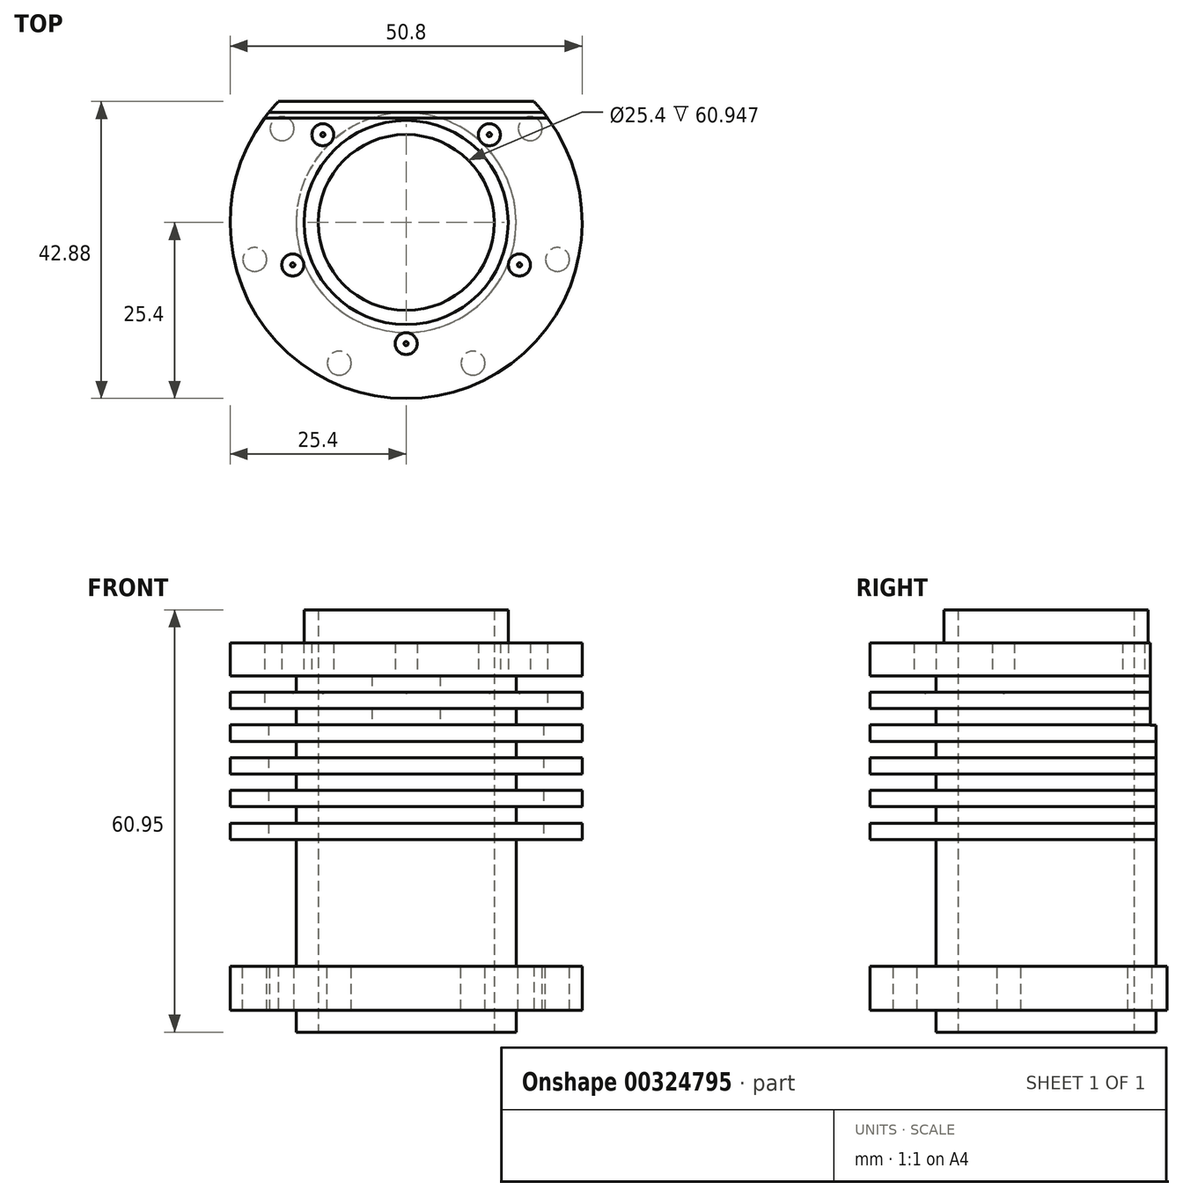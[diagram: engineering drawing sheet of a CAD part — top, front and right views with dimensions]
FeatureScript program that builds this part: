
annotation { "Feature Type Name" : "Feature", "Feature Type Description" : "" }
export const myFeature = defineFeature(function(context is Context, id is Id, definition is map)
    precondition{}
    {
        {
            var Q0;
            Q0=qCreatedBy(makeId("Top.planeOp"),FACE);
            var sketch = newSketch(context, id + "F0", { "sketchPlane" : qUnion([Q0])});
            skCircle(sketch, "E0", {"center": v(0, 0) * mm, "radius": 25.4 * mm});
            skSolve(sketch);
        }
        {
            var Q0;
            Q0=makeQuery(id+"F0.imprint","IMPRINT",FACE,{"disambiguationData":[TD([[makeQuery(id+"F0.imprint","IMPRINT",EDGE,{"derivedFrom":sQuery(id+"F0.wireOp",EDGE,"E0")}),1.0]])]});
            extrude(context, id + "F1", {"entities" : qUnion([Q0]), "depth" : 53 * mm, "offsetDistance" : 25.4 * mm});
        }
        {
            var Q0;
            Q0=makeQuery(id+"F1.opExtrude","CAP_FACE",FACE,{"disambiguationData":[OSD([sQuery(id+"F0.wireOp",EDGE,"E0")])],"isStart":false});
            var sketch = newSketch(context, id + "F2", { "sketchPlane" : qUnion([Q0])});
            skCircle(sketch, "E1", {"center": v(0, 0) * mm, "radius": 14.73 * mm});
            skSolve(sketch);
        }
        {
            var Q0;
            Q0=makeQuery(id+"F2.imprint","IMPRINT",FACE,{"disambiguationData":[TD([[makeQuery(id+"F2.imprint","IMPRINT",EDGE,{"derivedFrom":sQuery(id+"F2.wireOp",EDGE,"E1")}),1.0]])]});
            extrude(context, id + "F3", {"entities" : qUnion([Q0]), "operationType" : NewBodyOperationType.ADD, "depth" : 4.76 * mm, "offsetDistance" : 25.4 * mm});
        }
        {
            var Q0;
            Q0=makeQuery(id+"F1.opExtrude","CAP_FACE",FACE,{"disambiguationData":[OSD([sQuery(id+"F0.wireOp",EDGE,"E0")])],"isStart":true});
            var sketch = newSketch(context, id + "F4", { "sketchPlane" : qUnion([Q0])});
            skCircle(sketch, "E2", {"center": v(0, 0) * mm, "radius": 15.88 * mm});
            skSolve(sketch);
        }
        {
            var Q0;
            Q0=makeQuery(id+"F4.imprint","IMPRINT",FACE,{"disambiguationData":[TD([[makeQuery(id+"F4.imprint","IMPRINT",EDGE,{"derivedFrom":sQuery(id+"F4.wireOp",EDGE,"E2")}),1.0]])]});
            extrude(context, id + "F5", {"entities" : qUnion([Q0]), "operationType" : NewBodyOperationType.ADD, "depth" : 3.17 * mm, "offsetDistance" : 25.4 * mm});
        }
        {
            var Q0;
            Q0=makeQuery(id+"F5.opExtrude","CAP_FACE",FACE,{"disambiguationData":[OSD([sQuery(id+"F4.wireOp",EDGE,"E2")])],"isStart":false});
            var sketch = newSketch(context, id + "F6", { "sketchPlane" : qUnion([Q0])});
            skSolve(sketch);
        }
        {
            var Q0;
            Q0=makeQuery(id+"F6.imprint","IMPRINT",FACE,{"disambiguationData":[TD([[makeQuery(id+"F6.imprint","IMPRINT",EDGE,{"derivedFrom":makeQuery(id+"F5.opExtrude","CAP_EDGE",EDGE,{"disambiguationData":[OSD([sQuery(id+"F4.wireOp",EDGE,"E2")])],"isStart":false})}),1.0]])]});
            var sketch = newSketch(context, id + "F7", { "sketchPlane" : qUnion([Q0])});
            skCircle(sketch, "E3", {"center": v(0, 0) * mm, "radius": 12.7 * mm});
            skSolve(sketch);
        }
        {
            var Q0;
            Q0=makeQuery(id+"F7.imprint","IMPRINT",FACE,{"disambiguationData":[TD([[makeQuery(id+"F7.imprint","IMPRINT",EDGE,{"derivedFrom":sQuery(id+"F7.wireOp",EDGE,"E3")}),1.0]])]});
            extrude(context, id + "F8", {"entities" : qUnion([Q0]), "operationType" : NewBodyOperationType.REMOVE, "endBound" : BoundingType.THROUGH_ALL, "oppositeDirection" : true, "depth" : 25.4 * mm, "offsetDistance" : 25.4 * mm});
        }
        {
            var Q0;
            Q0=qCreatedBy(makeId("Front.planeOp"),FACE);
            var sketch = newSketch(context, id + "F9", { "sketchPlane" : qUnion([Q0])});
            skLineSegment(sketch, "E4", {"start": v(15.88, 63.37) * mm, "end": v(15.88, -10.47) * mm, "construction": true});
            skLineSegment(sketch, "E5", {"start": v(-43.89, 48.25) * mm, "end": v(39.02, 48.25) * mm, "construction": true});
            skLineSegment(sketch, "E6.bottom", {"start": v(15.88, 48.25) * mm, "end": v(28.02, 48.25) * mm});
            skLineSegment(sketch, "E6.top", {"start": v(15.88, 45.89) * mm, "end": v(28.02, 45.89) * mm});
            skLineSegment(sketch, "E6.left", {"start": v(15.88, 48.25) * mm, "end": v(15.88, 45.89) * mm});
            skLineSegment(sketch, "E6.right", {"start": v(28.02, 48.25) * mm, "end": v(28.02, 45.89) * mm});
            skLineSegment(sketch, "E7.1.0.0", {"start": v(15.88, 43.52) * mm, "end": v(28.02, 43.52) * mm});
            skLineSegment(sketch, "E7.1.0.1", {"start": v(15.88, 41.16) * mm, "end": v(28.02, 41.16) * mm});
            skLineSegment(sketch, "E7.1.0.2", {"start": v(15.88, 43.52) * mm, "end": v(15.88, 41.16) * mm});
            skLineSegment(sketch, "E7.1.0.3", {"start": v(28.02, 43.52) * mm, "end": v(28.02, 41.16) * mm});
            skLineSegment(sketch, "E7.2.0.0", {"start": v(15.88, 38.8) * mm, "end": v(28.02, 38.8) * mm});
            skLineSegment(sketch, "E7.2.0.1", {"start": v(15.88, 36.44) * mm, "end": v(28.02, 36.44) * mm});
            skLineSegment(sketch, "E7.2.0.2", {"start": v(15.88, 38.8) * mm, "end": v(15.88, 36.44) * mm});
            skLineSegment(sketch, "E7.2.0.3", {"start": v(28.02, 38.8) * mm, "end": v(28.02, 36.44) * mm});
            skLineSegment(sketch, "E7.3.0.0", {"start": v(15.88, 34.07) * mm, "end": v(28.02, 34.07) * mm});
            skLineSegment(sketch, "E7.3.0.1", {"start": v(15.88, 31.71) * mm, "end": v(28.02, 31.71) * mm});
            skLineSegment(sketch, "E7.3.0.2", {"start": v(15.88, 34.07) * mm, "end": v(15.88, 31.71) * mm});
            skLineSegment(sketch, "E7.3.0.3", {"start": v(28.02, 34.07) * mm, "end": v(28.02, 31.71) * mm});
            skLineSegment(sketch, "E7.4.0.0", {"start": v(15.88, 29.35) * mm, "end": v(28.02, 29.35) * mm});
            skLineSegment(sketch, "E7.4.0.1", {"start": v(15.88, 26.99) * mm, "end": v(28.02, 26.99) * mm});
            skLineSegment(sketch, "E7.4.0.2", {"start": v(15.88, 29.35) * mm, "end": v(15.88, 26.99) * mm});
            skLineSegment(sketch, "E7.4.0.3", {"start": v(28.02, 29.35) * mm, "end": v(28.02, 26.99) * mm});
            skLineSegment(sketch, "E7.direction1", {"start": v(15.88, 45.89) * mm, "end": v(15.88, 41.16) * mm, "construction": true});
            skLineSegment(sketch, "E8", {"start": v(-27.72, 6.35) * mm, "end": v(31.12, 6.35) * mm, "construction": true});
            skLineSegment(sketch, "E9", {"start": v(15.88, 24.63) * mm, "end": v(15.88, 6.35) * mm});
            skLineSegment(sketch, "E10", {"start": v(15.88, 6.35) * mm, "end": v(28.98, 6.35) * mm});
            skSolve(sketch);
        }
        {
            var Q0;
            Q0=makeQuery(id+"F9.imprint","IMPRINT",FACE,{"disambiguationData":[TD([[makeQuery(id+"F9.imprint","IMPRINT",EDGE,{"derivedFrom":sQuery(id+"F9.wireOp",EDGE,"E6.bottom")}),-1.0]])]});
            var Q1;
            Q1=makeQuery(id+"F9.imprint","IMPRINT",FACE,{"disambiguationData":[TD([[makeQuery(id+"F9.imprint","IMPRINT",EDGE,{"derivedFrom":sQuery(id+"F9.wireOp",EDGE,"E7.1.0.0")}),-1.0]])]});
            var Q2;
            Q2=makeQuery(id+"F9.imprint","IMPRINT",FACE,{"disambiguationData":[TD([[makeQuery(id+"F9.imprint","IMPRINT",EDGE,{"derivedFrom":sQuery(id+"F9.wireOp",EDGE,"E7.2.0.0")}),-1.0]])]});
            var Q3;
            Q3=makeQuery(id+"F9.imprint","IMPRINT",FACE,{"disambiguationData":[TD([[makeQuery(id+"F9.imprint","IMPRINT",EDGE,{"derivedFrom":sQuery(id+"F9.wireOp",EDGE,"E7.3.0.0")}),-1.0]])]});
            var Q4;
            Q4=makeQuery(id+"F9.imprint","IMPRINT",FACE,{"disambiguationData":[TD([[makeQuery(id+"F9.imprint","IMPRINT",EDGE,{"derivedFrom":sQuery(id+"F9.wireOp",EDGE,"E7.4.0.0")}),-1.0]])]});
            var Q5;
            Q5=makeQuery(id+"F9.imprint","IMPRINT",FACE,{"disambiguationData":[TD([[makeQuery(id+"F9.imprint","IMPRINT",EDGE,{"derivedFrom":sQuery(id+"F9.wireOp",EDGE,"e0e7658a-f0d1-407f-a81c-850310b283b5.0.5.0")}),-1.0]])]});
            var Q6;
            Q6=makeQuery(id+"F1.opExtrude","SWEPT_FACE",FACE,{"disambiguationData":[OSD([sQuery(id+"F0.wireOp",EDGE,"E0")])]});
            revolve(context, id + "F10", {"operationType" : NewBodyOperationType.REMOVE, "entities" : qUnion([Q0, Q1, Q2, Q3, Q4, Q5]), "axis" : qUnion([Q6]), "revolveType" : RevolveType.FULL, "oppositeDirection" : true});
        }
        {
            var Q0;
            Q0=qCreatedBy(makeId("Front.planeOp"),FACE);
            var sketch = newSketch(context, id + "F11", { "sketchPlane" : qUnion([Q0])});
            skLineSegment(sketch, "E11", {"start": v(-39.25, 6.35) * mm, "end": v(35.32, 6.35) * mm, "construction": true});
            skLineSegment(sketch, "E12", {"start": v(-28.17, 24.63) * mm, "end": v(30.33, 24.63) * mm, "construction": true});
            skLineSegment(sketch, "E13", {"start": v(15.87, 28.26) * mm, "end": v(15.88, -4.44) * mm, "construction": true});
            skLineSegment(sketch, "E14.bottom", {"start": v(15.88, 24.63) * mm, "end": v(29.2, 24.63) * mm});
            skLineSegment(sketch, "E14.top", {"start": v(15.88, 6.35) * mm, "end": v(29.2, 6.35) * mm});
            skLineSegment(sketch, "E14.left", {"start": v(15.88, 24.63) * mm, "end": v(15.88, 6.35) * mm});
            skLineSegment(sketch, "E14.right", {"start": v(29.2, 24.63) * mm, "end": v(29.2, 6.35) * mm});
            skSolve(sketch);
        }
        {
            var Q0;
            Q0=makeQuery(id+"F11.imprint","IMPRINT",FACE,{"disambiguationData":[TD([[makeQuery(id+"F11.imprint","IMPRINT",EDGE,{"derivedFrom":sQuery(id+"F11.wireOp",EDGE,"E14.bottom")}),-1.0]])]});
            var Q1;
            {var subQ0=sQuery(id+"F0.wireOp",EDGE,"E0");Q1=makeQuery(id+"F10.boolean.opBoolean","SPLIT",FACE,{"disambiguationData":[TD([makeQuery(id+"F1.opExtrude","CAP_FACE",FACE,{"disambiguationData":[OSD([subQ0])],"isStart":true})])],"derivedFrom":makeQuery(id+"F1.opExtrude","SWEPT_FACE",FACE,{"disambiguationData":[OSD([subQ0])]})});}
            revolve(context, id + "F12", {"operationType" : NewBodyOperationType.REMOVE, "entities" : qUnion([Q0]), "axis" : qUnion([Q1]), "revolveType" : RevolveType.FULL, "oppositeDirection" : true});
        }
        {
            var Q0;
            Q0=makeQuery(id+"F1.opExtrude","CAP_FACE",FACE,{"disambiguationData":[OSD([sQuery(id+"F0.wireOp",EDGE,"E0")])],"isStart":false});
            var sketch = newSketch(context, id + "F13", { "sketchPlane" : qUnion([Q0])});
            skLineSegment(sketch, "E15.bottom", {"start": v(-28.86, 15.09) * mm, "end": v(35.5, 15.09) * mm});
            skLineSegment(sketch, "E15.top", {"start": v(-28.86, 32.1) * mm, "end": v(35.5, 32.1) * mm});
            skLineSegment(sketch, "E15.left", {"start": v(-28.86, 15.09) * mm, "end": v(-28.86, 32.1) * mm});
            skLineSegment(sketch, "E15.right", {"start": v(35.5, 15.09) * mm, "end": v(35.5, 32.1) * mm});
            skSolve(sketch);
        }
        {
            var Q0;
            Q0=makeQuery(id+"F13.imprint","IMPRINT",FACE,{"disambiguationData":[TD([[makeQuery(id+"F13.imprint","IMPRINT",EDGE,{"derivedFrom":sQuery(id+"F13.wireOp",EDGE,"E15.top")}),-1.0]])]});
            var Q1;
            {var subQ0=sQuery(id+"F13.wireOp",EDGE,"E15.bottom");var subQ1=makeQuery(id+"F1.opExtrude","CAP_EDGE",EDGE,{"disambiguationData":[OSD([sQuery(id+"F0.wireOp",EDGE,"E0")])],"isStart":false});var subQ2=makeQuery(id+"F13.imprint","INTERSECT",VERTEX,{"disambiguationData":[OD(0.0)],"derivedFrom":[subQ1,subQ0]});Q1=makeQuery(id+"F13.imprint","IMPRINT",FACE,{"disambiguationData":[TD([[makeQuery(id+"F13.imprint","IMPRINT",EDGE,{"disambiguationData":[TD([[subQ2,-1.0]])],"derivedFrom":subQ0}),1.0]])]});}
            extrude(context, id + "F14", {"entities" : qUnion([Q0, Q1]), "operationType" : NewBodyOperationType.REMOVE, "oppositeDirection" : true, "depth" : 11.86 * mm, "offsetDistance" : 25.4 * mm});
        }
        {
            var Q0;
            Q0=makeQuery(id+"F14.boolean.opBoolean","COPY",FACE,{"derivedFrom":makeQuery(id+"F14.opExtrude","CAP_FACE",FACE,{"disambiguationData":[OSD([sQuery(id+"F13.wireOp",EDGE,"E15.bottom"),sQuery(id+"F13.wireOp",EDGE,"E15.top"),sQuery(id+"F13.wireOp",EDGE,"E15.left"),sQuery(id+"F13.wireOp",EDGE,"E15.right")])],"isStart":false})});
            var sketch = newSketch(context, id + "F15", { "sketchPlane" : qUnion([Q0])});
            skLineSegment(sketch, "E16.bottom", {"start": v(-23.48, 25.8) * mm, "end": v(22.7, 25.8) * mm});
            skLineSegment(sketch, "E16.top", {"start": v(-23.48, 15.88) * mm, "end": v(22.7, 15.88) * mm});
            skLineSegment(sketch, "E16.left", {"start": v(-23.48, 25.8) * mm, "end": v(-23.48, 15.88) * mm});
            skLineSegment(sketch, "E16.right", {"start": v(22.7, 25.8) * mm, "end": v(22.7, 15.88) * mm});
            skSolve(sketch);
        }
        {
            var Q0;
            Q0=makeQuery(id+"F15.imprint","IMPRINT",FACE,{"disambiguationData":[TD([[makeQuery(id+"F15.imprint","IMPRINT",EDGE,{"derivedFrom":sQuery(id+"F15.wireOp",EDGE,"E16.bottom")}),-1.0]])]});
            var Q1;
            {var subQ0=sQuery(id+"F15.wireOp",EDGE,"E16.top");var subQ1=makeQuery(id+"F14.boolean.opBoolean","INTERSECT",EDGE,{"derivedFrom":[makeQuery(id+"F10.boolean.opBoolean","SPLIT",FACE,{"disambiguationData":[TD([makeQuery(id+"F10.opRevolve","SWEPT_FACE",FACE,{"disambiguationData":[OSD([sQuery(id+"F9.wireOp",EDGE,"E7.1.0.1")])]})])],"derivedFrom":makeQuery(id+"F1.opExtrude","SWEPT_FACE",FACE,{"disambiguationData":[OSD([sQuery(id+"F0.wireOp",EDGE,"E0")])]})}),makeQuery(id+"F14.opExtrude","CAP_FACE",FACE,{"disambiguationData":[OSD([sQuery(id+"F13.wireOp",EDGE,"E15.bottom"),sQuery(id+"F13.wireOp",EDGE,"E15.top"),sQuery(id+"F13.wireOp",EDGE,"E15.left"),sQuery(id+"F13.wireOp",EDGE,"E15.right")])],"isStart":false})]});var subQ2=makeQuery(id+"F15.imprint","INTERSECT",VERTEX,{"disambiguationData":[OD(0.0)],"derivedFrom":[subQ1,subQ0]});Q1=makeQuery(id+"F15.imprint","IMPRINT",FACE,{"disambiguationData":[TD([[makeQuery(id+"F15.imprint","IMPRINT",EDGE,{"disambiguationData":[TD([[subQ2,-1.0]])],"derivedFrom":subQ0}),1.0]])]});}
            extrude(context, id + "F16", {"entities" : qUnion([Q0, Q1]), "operationType" : NewBodyOperationType.REMOVE, "oppositeDirection" : true, "depth" : 16.64 * mm, "offsetDistance" : 25.4 * mm});
        }
        {
            var Q0;
            Q0=makeQuery(id+"F1.opExtrude","CAP_FACE",FACE,{"disambiguationData":[OSD([sQuery(id+"F0.wireOp",EDGE,"E0")])],"isStart":true});
            var sketch = newSketch(context, id + "F17", { "sketchPlane" : qUnion([Q0])});
            skLineSegment(sketch, "E17.bottom", {"start": v(-34.07, -17.48) * mm, "end": v(38.07, -17.48) * mm});
            skLineSegment(sketch, "E17.top", {"start": v(-34.07, -39.26) * mm, "end": v(38.07, -39.26) * mm});
            skLineSegment(sketch, "E17.left", {"start": v(-34.07, -17.48) * mm, "end": v(-34.07, -39.26) * mm});
            skLineSegment(sketch, "E17.right", {"start": v(38.07, -17.48) * mm, "end": v(38.07, -39.26) * mm});
            skSolve(sketch);
        }
        {
            var Q0;
            Q0=makeQuery(id+"F17.imprint","IMPRINT",FACE,{"disambiguationData":[TD([[makeQuery(id+"F17.imprint","IMPRINT",EDGE,{"derivedFrom":sQuery(id+"F17.wireOp",EDGE,"E17.top")}),1.0]])]});
            var Q1;
            {var subQ0=sQuery(id+"F17.wireOp",EDGE,"E17.bottom");var subQ1=makeQuery(id+"F1.opExtrude","CAP_EDGE",EDGE,{"disambiguationData":[OSD([sQuery(id+"F0.wireOp",EDGE,"E0")])],"isStart":true});var subQ2=makeQuery(id+"F17.imprint","INTERSECT",VERTEX,{"disambiguationData":[OD(0.0)],"derivedFrom":[subQ1,subQ0]});Q1=makeQuery(id+"F17.imprint","IMPRINT",FACE,{"disambiguationData":[TD([[makeQuery(id+"F17.imprint","IMPRINT",EDGE,{"disambiguationData":[TD([[subQ2,-1.0]])],"derivedFrom":subQ0}),-1.0]])]});}
            extrude(context, id + "F18", {"entities" : qUnion([Q0, Q1]), "operationType" : NewBodyOperationType.REMOVE, "oppositeDirection" : true, "depth" : 6.48 * mm, "offsetDistance" : 25.4 * mm});
        }
        {
            var Q0;
            Q0=makeQuery(id+"F1.opExtrude","CAP_FACE",FACE,{"disambiguationData":[OSD([sQuery(id+"F0.wireOp",EDGE,"E0")])],"isStart":true});
            var sketch = newSketch(context, id + "F19", { "sketchPlane" : qUnion([Q0])});
            skPoint(sketch, "E18", {"position": v(-17.9, -13.56) * mm});
            skPoint(sketch, "E19", {"position": v(17.9, -13.56) * mm});
            skPoint(sketch, "E20", {"position": v(-21.84, 5.33) * mm});
            skPoint(sketch, "E21", {"position": v(21.84, 5.33) * mm});
            skPoint(sketch, "E22", {"position": v(-9.65, 20.3) * mm});
            skPoint(sketch, "E23", {"position": v(9.65, 20.3) * mm});
            skSolve(sketch);
        }
        {
            var Q0;
            Q0=sQuery(id+"F19.wireOp",VERTEX,"E18");
            var Q1;
            Q1=sQuery(id+"F19.wireOp",VERTEX,"E20");
            var Q2;
            Q2=sQuery(id+"F19.wireOp",VERTEX,"E22");
            var Q3;
            Q3=sQuery(id+"F19.wireOp",VERTEX,"E23");
            var Q4;
            Q4=sQuery(id+"F19.wireOp",VERTEX,"E21");
            var Q5;
            Q5=sQuery(id+"F19.wireOp",VERTEX,"E19");
            var Q6;
            Q6=makeQuery(id+"F1.opExtrude","SWEPT_BODY",BODY,{"disambiguationData":[OSD([sQuery(id+"F0.wireOp",EDGE,"E0")])]});
            hole(context, id + "F20", {"style" : HoleStyle.SIMPLE, "endStyle" : HoleEndStyle.BLIND, "holeDiameter" : 3.45 * mm, "majorDiameter" : 6.35 * mm, "holeDepth" : 7.62 * mm, "tappedDepth" : 12.7 * mm, "tapClearance" : 3, "locations" : qUnion([Q0, Q1, Q2, Q3, Q4, Q5]), "scope" : qUnion([Q6])});
        }
        {
            var Q0;
            Q0=makeQuery(id+"F1.opExtrude","CAP_FACE",FACE,{"disambiguationData":[OSD([sQuery(id+"F0.wireOp",EDGE,"E0")])],"isStart":false});
            var sketch = newSketch(context, id + "F21", { "sketchPlane" : qUnion([Q0])});
            skPoint(sketch, "E24", {"position": v(-16.36, -6.12) * mm});
            skPoint(sketch, "E25", {"position": v(16.36, -6.12) * mm});
            skPoint(sketch, "E26", {"position": v(-12.01, 12.67) * mm});
            skPoint(sketch, "E27", {"position": v(12.01, 12.67) * mm});
            skPoint(sketch, "E28", {"position": v(0, -17.48) * mm});
            skSolve(sketch);
        }
        {
            var Q0;
            Q0=sQuery(id+"F21.wireOp",VERTEX,"E26");
            var Q1;
            Q1=sQuery(id+"F21.wireOp",VERTEX,"E27");
            var Q2;
            Q2=sQuery(id+"F21.wireOp",VERTEX,"E25");
            var Q3;
            Q3=sQuery(id+"F21.wireOp",VERTEX,"E24");
            var Q4;
            Q4=sQuery(id+"F21.wireOp",VERTEX,"E28");
            var Q5;
            Q5=makeQuery(id+"F1.opExtrude","SWEPT_BODY",BODY,{"disambiguationData":[OSD([sQuery(id+"F0.wireOp",EDGE,"E0")])]});
            hole(context, id + "F22", {"style" : HoleStyle.SIMPLE, "endStyle" : HoleEndStyle.BLIND, "holeDiameter" : 3.17 * mm, "majorDiameter" : 6.35 * mm, "holeDepth" : 6.35 * mm, "tappedDepth" : 12.7 * mm, "tapClearance" : 3, "locations" : qUnion([Q0, Q1, Q2, Q3, Q4]), "scope" : qUnion([Q5])});
        }
    });
